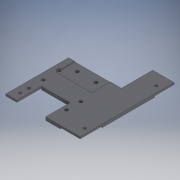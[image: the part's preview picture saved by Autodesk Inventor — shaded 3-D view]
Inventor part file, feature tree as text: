
AUTODESK INVENTOR PART (.ipt)
format: ipt  version: 2018 (Build 220112000, 112)  size: 195,072 bytes
history: native  units: mm
features: extrude x4, thread x4, sketch x4
ambient origin geometry x8: Origin, YZ Plane, XZ Plane, XY Plane, X Axis, Y Axis, Z Axis, Center Point
bodies: Solid1 (feature_tree)
feature tree (12):
  extrude  "Extrusion1"  Depth=60.0mm
  extrude  "Extrusion2"  Depth=90.0mm
  extrude  "Extrusion3"  Depth=300.0mm
  thread  "Thread1"  [1 undecoded]
  thread  "Thread2"  [1 undecoded]
  thread  "Thread3"  [1 undecoded]
  thread  "Thread4"  [1 undecoded]
  extrude  "Extrusion4"  Depth=70.5mm
  sketch  "Sketch1"  dims[d82=10.0mm d83=60.0mm]
  sketch  "Sketch2"  dims[d86=32.0mm d87=90.0mm]
  sketch  "Sketch3"  dims[d88=92.0mm d90=300.0mm d91=200.0mm d92=35.0mm d93=68.0mm d94=100.0mm]
  sketch  "Sketch4"  dims[d95=237.0mm d96=79.0mm d98=60.0mm d100=46.0mm d101=8.5mm d102=140.0mm d103=80.0mm d104=3.0mm d105=152.0mm d106=61.0mm d107=85.0mm d108=40.0mm d109=10.0mm d110=0.0mm d111=114.0mm d112=60.0mm d113=20.0mm d114=1.5mm d115=0.0mm d116=14.0mm d117=1.5mm d118=0.0mm d119=10.0mm d120=0.0mm d121=10.0mm d122=0.0mm d123=10.0mm d124=0.0mm d125=10.0mm d126=0.0mm d127=66.0mm d128=62.0mm d129=90.0deg d130=66.0mm d131=90.0deg d132=4.0mm d133=0.0mm d134=64.0mm d135=70.5mm d136=12.0mm]
note: 4 required parameter values undecoded (feature->parameter linkage not recoverable at this tier; creation-order binding heuristic only, values carry confidence <= 0.55)
